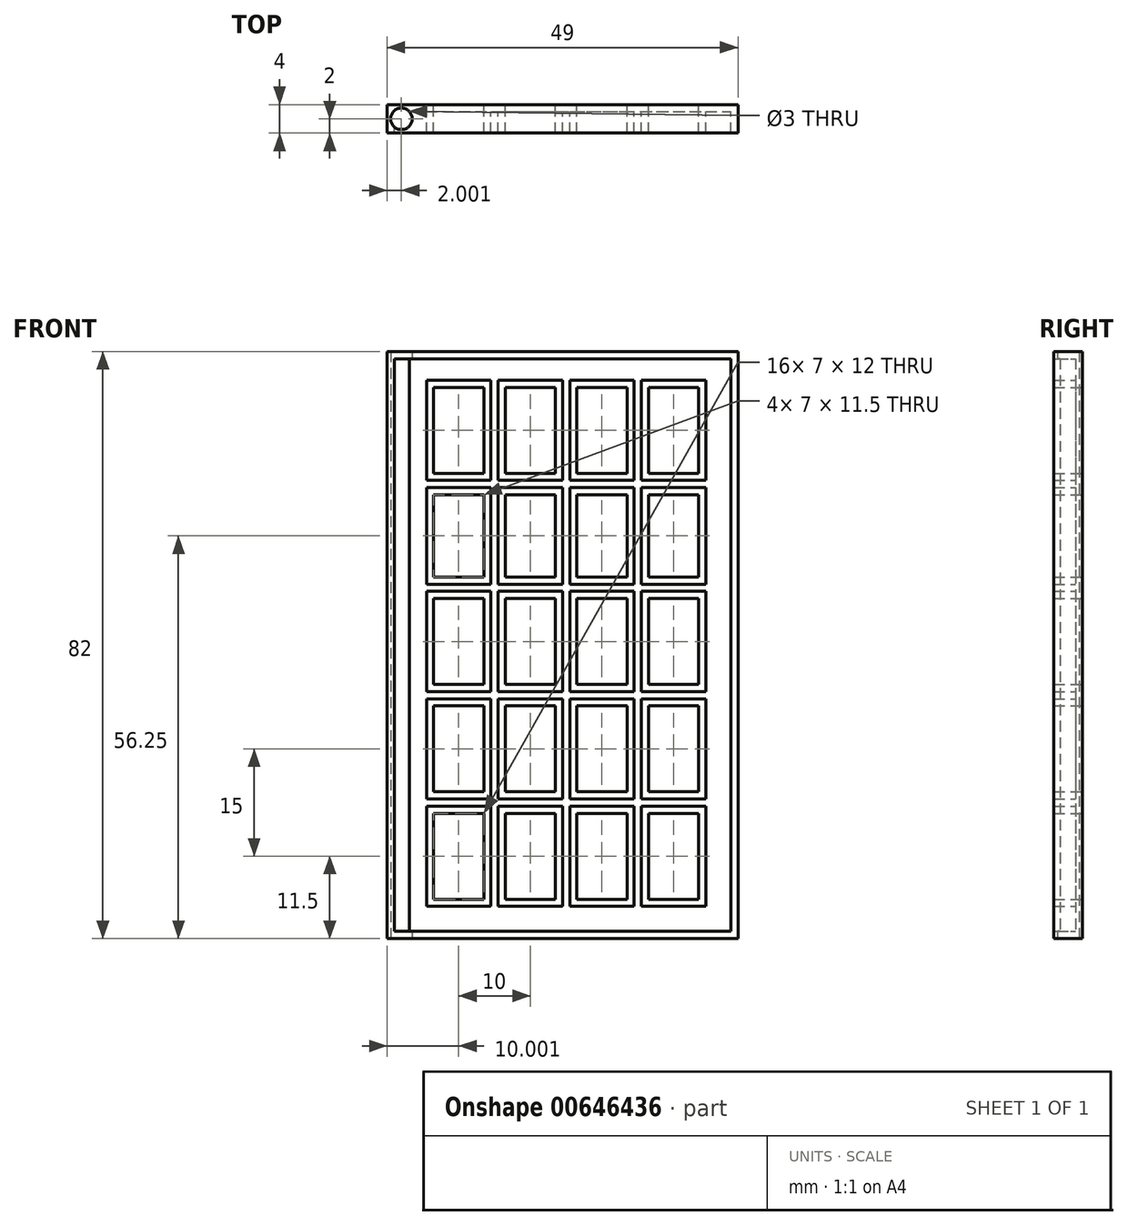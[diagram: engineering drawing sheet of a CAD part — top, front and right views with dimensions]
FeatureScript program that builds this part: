
annotation { "Feature Type Name" : "Feature", "Feature Type Description" : "" }
export const myFeature = defineFeature(function(context is Context, id is Id, definition is map)
    precondition{}
    {
        {
            var Q0;
            Q0=qCreatedBy(makeId("Front.planeOp"),FACE);
            var sketch = newSketch(context, id + "F0", { "sketchPlane" : qUnion([Q0])});
            skLineSegment(sketch, "E0.bottom", {"start": v(9.11, 82) * mm, "end": v(58.11, 82) * mm});
            skLineSegment(sketch, "E0.top", {"start": v(9.11, 0) * mm, "end": v(58.11, 0) * mm});
            skLineSegment(sketch, "E0.left", {"start": v(9.11, 82) * mm, "end": v(9.11, 0) * mm});
            skLineSegment(sketch, "E0.right", {"start": v(58.11, 82) * mm, "end": v(58.11, 0) * mm});
            skLineSegment(sketch, "E1.bottom", {"start": v(14.11, 78) * mm, "end": v(54.11, 78) * mm});
            skLineSegment(sketch, "E1.top", {"start": v(14.11, 4) * mm, "end": v(54.11, 4) * mm});
            skLineSegment(sketch, "E1.left", {"start": v(14.11, 78) * mm, "end": v(14.11, 4) * mm});
            skLineSegment(sketch, "E1.right", {"start": v(54.11, 78) * mm, "end": v(54.11, 4) * mm});
            skLineSegment(sketch, "E2.bottom", {"start": v(25.61, 77) * mm, "end": v(32.61, 77) * mm});
            skLineSegment(sketch, "E2.top", {"start": v(25.61, 65) * mm, "end": v(32.61, 65) * mm});
            skLineSegment(sketch, "E2.left", {"start": v(25.61, 77) * mm, "end": v(25.61, 65) * mm});
            skLineSegment(sketch, "E2.right", {"start": v(32.61, 77) * mm, "end": v(32.61, 65) * mm});
            skLineSegment(sketch, "E3.bottom", {"start": v(35.61, 77) * mm, "end": v(42.61, 77) * mm});
            skLineSegment(sketch, "E3.top", {"start": v(35.61, 65) * mm, "end": v(42.61, 65) * mm});
            skLineSegment(sketch, "E3.left", {"start": v(35.61, 77) * mm, "end": v(35.61, 65) * mm});
            skLineSegment(sketch, "E3.right", {"start": v(42.61, 77) * mm, "end": v(42.61, 65) * mm});
            skLineSegment(sketch, "E4.bottom", {"start": v(45.61, 77) * mm, "end": v(52.61, 77) * mm});
            skLineSegment(sketch, "E4.top", {"start": v(45.61, 65) * mm, "end": v(52.61, 65) * mm});
            skLineSegment(sketch, "E4.left", {"start": v(45.61, 77) * mm, "end": v(45.61, 65) * mm});
            skLineSegment(sketch, "E4.right", {"start": v(52.61, 77) * mm, "end": v(52.61, 65) * mm});
            skLineSegment(sketch, "E5.bottom", {"start": v(15.61, 77) * mm, "end": v(22.61, 77) * mm});
            skLineSegment(sketch, "E5.top", {"start": v(15.61, 65) * mm, "end": v(22.61, 65) * mm});
            skLineSegment(sketch, "E5.left", {"start": v(15.61, 77) * mm, "end": v(15.61, 65) * mm});
            skLineSegment(sketch, "E5.right", {"start": v(22.61, 77) * mm, "end": v(22.61, 65) * mm});
            skLineSegment(sketch, "E6.bottom", {"start": v(15.61, 62) * mm, "end": v(22.61, 62) * mm});
            skLineSegment(sketch, "E6.top", {"start": v(15.61, 50.5) * mm, "end": v(22.61, 50.5) * mm});
            skLineSegment(sketch, "E6.left", {"start": v(15.61, 62) * mm, "end": v(15.61, 50.5) * mm});
            skLineSegment(sketch, "E6.right", {"start": v(22.61, 62) * mm, "end": v(22.61, 50.5) * mm});
            skLineSegment(sketch, "E7.bottom", {"start": v(25.61, 62) * mm, "end": v(32.61, 62) * mm});
            skLineSegment(sketch, "E7.top", {"start": v(25.61, 50.5) * mm, "end": v(32.61, 50.5) * mm});
            skLineSegment(sketch, "E7.left", {"start": v(25.61, 62) * mm, "end": v(25.61, 50.5) * mm});
            skLineSegment(sketch, "E7.right", {"start": v(32.61, 62) * mm, "end": v(32.61, 50.5) * mm});
            skLineSegment(sketch, "E8.bottom", {"start": v(35.61, 62) * mm, "end": v(42.61, 62) * mm});
            skLineSegment(sketch, "E8.top", {"start": v(35.61, 50.5) * mm, "end": v(42.61, 50.5) * mm});
            skLineSegment(sketch, "E8.left", {"start": v(35.61, 62) * mm, "end": v(35.61, 50.5) * mm});
            skLineSegment(sketch, "E8.right", {"start": v(42.61, 62) * mm, "end": v(42.61, 50.5) * mm});
            skLineSegment(sketch, "E9.bottom", {"start": v(45.61, 62) * mm, "end": v(52.61, 62) * mm});
            skLineSegment(sketch, "E9.top", {"start": v(45.61, 50.5) * mm, "end": v(52.61, 50.5) * mm});
            skLineSegment(sketch, "E9.left", {"start": v(45.61, 62) * mm, "end": v(45.61, 50.5) * mm});
            skLineSegment(sketch, "E9.right", {"start": v(52.61, 62) * mm, "end": v(52.61, 50.5) * mm});
            skLineSegment(sketch, "E10.bottom", {"start": v(15.61, 47.5) * mm, "end": v(22.61, 47.5) * mm});
            skLineSegment(sketch, "E10.top", {"start": v(15.61, 35.5) * mm, "end": v(22.61, 35.5) * mm});
            skLineSegment(sketch, "E10.left", {"start": v(15.61, 47.5) * mm, "end": v(15.61, 35.5) * mm});
            skLineSegment(sketch, "E10.right", {"start": v(22.61, 47.5) * mm, "end": v(22.61, 35.5) * mm});
            skLineSegment(sketch, "E11.bottom", {"start": v(25.61, 47.5) * mm, "end": v(32.61, 47.5) * mm});
            skLineSegment(sketch, "E11.top", {"start": v(25.61, 35.5) * mm, "end": v(32.61, 35.5) * mm});
            skLineSegment(sketch, "E11.left", {"start": v(25.61, 47.5) * mm, "end": v(25.61, 35.5) * mm});
            skLineSegment(sketch, "E11.right", {"start": v(32.61, 47.5) * mm, "end": v(32.61, 35.5) * mm});
            skLineSegment(sketch, "E12.bottom", {"start": v(35.61, 47.5) * mm, "end": v(42.61, 47.5) * mm});
            skLineSegment(sketch, "E12.top", {"start": v(35.61, 35.5) * mm, "end": v(42.61, 35.5) * mm});
            skLineSegment(sketch, "E12.left", {"start": v(35.61, 47.5) * mm, "end": v(35.61, 35.5) * mm});
            skLineSegment(sketch, "E12.right", {"start": v(42.61, 47.5) * mm, "end": v(42.61, 35.5) * mm});
            skLineSegment(sketch, "E13.bottom", {"start": v(45.61, 47.5) * mm, "end": v(52.61, 47.5) * mm});
            skLineSegment(sketch, "E13.top", {"start": v(45.61, 35.5) * mm, "end": v(52.61, 35.5) * mm});
            skLineSegment(sketch, "E13.left", {"start": v(45.61, 47.5) * mm, "end": v(45.61, 35.5) * mm});
            skLineSegment(sketch, "E13.right", {"start": v(52.61, 47.5) * mm, "end": v(52.61, 35.5) * mm});
            skLineSegment(sketch, "E14.bottom", {"start": v(15.61, 32.5) * mm, "end": v(22.61, 32.5) * mm});
            skLineSegment(sketch, "E14.top", {"start": v(15.61, 20.5) * mm, "end": v(22.61, 20.5) * mm});
            skLineSegment(sketch, "E14.left", {"start": v(15.61, 32.5) * mm, "end": v(15.61, 20.5) * mm});
            skLineSegment(sketch, "E14.right", {"start": v(22.61, 32.5) * mm, "end": v(22.61, 20.5) * mm});
            skLineSegment(sketch, "E15.bottom", {"start": v(25.61, 32.5) * mm, "end": v(32.61, 32.5) * mm});
            skLineSegment(sketch, "E15.top", {"start": v(25.61, 20.5) * mm, "end": v(32.61, 20.5) * mm});
            skLineSegment(sketch, "E15.left", {"start": v(25.61, 32.5) * mm, "end": v(25.61, 20.5) * mm});
            skLineSegment(sketch, "E15.right", {"start": v(32.61, 32.5) * mm, "end": v(32.61, 20.5) * mm});
            skLineSegment(sketch, "E16.bottom", {"start": v(35.61, 32.5) * mm, "end": v(42.61, 32.5) * mm});
            skLineSegment(sketch, "E16.top", {"start": v(35.61, 20.5) * mm, "end": v(42.61, 20.5) * mm});
            skLineSegment(sketch, "E16.left", {"start": v(35.61, 32.5) * mm, "end": v(35.61, 20.5) * mm});
            skLineSegment(sketch, "E16.right", {"start": v(42.61, 32.5) * mm, "end": v(42.61, 20.5) * mm});
            skLineSegment(sketch, "E17.bottom", {"start": v(45.61, 32.5) * mm, "end": v(52.61, 32.5) * mm});
            skLineSegment(sketch, "E17.top", {"start": v(45.61, 20.5) * mm, "end": v(52.61, 20.5) * mm});
            skLineSegment(sketch, "E17.left", {"start": v(45.61, 32.5) * mm, "end": v(45.61, 20.5) * mm});
            skLineSegment(sketch, "E17.right", {"start": v(52.61, 32.5) * mm, "end": v(52.61, 20.5) * mm});
            skLineSegment(sketch, "E18.bottom", {"start": v(15.61, 17.5) * mm, "end": v(22.61, 17.5) * mm});
            skLineSegment(sketch, "E18.top", {"start": v(15.61, 5.5) * mm, "end": v(22.61, 5.5) * mm});
            skLineSegment(sketch, "E18.left", {"start": v(15.61, 17.5) * mm, "end": v(15.61, 5.5) * mm});
            skLineSegment(sketch, "E18.right", {"start": v(22.61, 17.5) * mm, "end": v(22.61, 5.5) * mm});
            skLineSegment(sketch, "E19.bottom", {"start": v(25.61, 17.5) * mm, "end": v(32.61, 17.5) * mm});
            skLineSegment(sketch, "E19.top", {"start": v(25.61, 5.5) * mm, "end": v(32.61, 5.5) * mm});
            skLineSegment(sketch, "E19.left", {"start": v(25.61, 17.5) * mm, "end": v(25.61, 5.5) * mm});
            skLineSegment(sketch, "E19.right", {"start": v(32.61, 17.5) * mm, "end": v(32.61, 5.5) * mm});
            skLineSegment(sketch, "E20.bottom", {"start": v(35.61, 17.5) * mm, "end": v(42.61, 17.5) * mm});
            skLineSegment(sketch, "E20.top", {"start": v(35.61, 5.5) * mm, "end": v(42.61, 5.5) * mm});
            skLineSegment(sketch, "E20.left", {"start": v(35.61, 17.5) * mm, "end": v(35.61, 5.5) * mm});
            skLineSegment(sketch, "E20.right", {"start": v(42.61, 17.5) * mm, "end": v(42.61, 5.5) * mm});
            skLineSegment(sketch, "E21.bottom", {"start": v(45.61, 17.5) * mm, "end": v(52.61, 17.5) * mm});
            skLineSegment(sketch, "E21.top", {"start": v(45.61, 5.5) * mm, "end": v(52.61, 5.5) * mm});
            skLineSegment(sketch, "E21.left", {"start": v(45.61, 17.5) * mm, "end": v(45.61, 5.5) * mm});
            skLineSegment(sketch, "E21.right", {"start": v(52.61, 17.5) * mm, "end": v(52.61, 5.5) * mm});
            skSolve(sketch);
        }
        {
            var Q0;
            {var subQ0=sQuery(id+"F0.wireOp",EDGE,"95jugb8S-jBrk-O8sG-tFiF-yQ4KkkH1rrNL");Q0=makeQuery(id+"F0.imprint","IMPRINT",FACE,{"disambiguationData":[TD([[makeQuery(id+"F0.imprint","IMPRINT",EDGE,{"derivedFrom":subQ0}),-1.0]])]});}
            var Q1;
            {var subQ0=sQuery(id+"F0.wireOp",EDGE,"Lh07aYga-HaEd-fFaN-Omj2-mk0DnxkQiKFK");Q1=makeQuery(id+"F0.imprint","IMPRINT",FACE,{"disambiguationData":[TD([[makeQuery(id+"F0.imprint","IMPRINT",EDGE,{"derivedFrom":subQ0}),1.0]])]});}
            var Q2;
            {var subQ0=sQuery(id+"F0.wireOp",EDGE,"E1.bottom");Q2=makeQuery(id+"F0.imprint","IMPRINT",FACE,{"disambiguationData":[TD([[makeQuery(id+"F0.imprint","IMPRINT",EDGE,{"derivedFrom":subQ0}),-1.0]])]});}
            var Q3;
            Q3=makeQuery(id+"F0.imprint","IMPRINT",FACE,{"disambiguationData":[TD([[makeQuery(id+"F0.imprint","IMPRINT",EDGE,{"derivedFrom":sQuery(id+"F0.wireOp",EDGE,"E0.bottom")}),-1.0]])]});
            extrude(context, id + "F1", {"entities" : qUnion([Q0, Q1, Q2, Q3]), "depth" : 4 * mm, "offsetDistance" : 25 * mm});
        }
        {
            var Q0;
            Q0=makeQuery(id+"F1.opExtrude","CAP_FACE",FACE,{"disambiguationData":[OSD([sQuery(id+"F0.wireOp",EDGE,"E0.bottom"),sQuery(id+"F0.wireOp",EDGE,"E0.top"),sQuery(id+"F0.wireOp",EDGE,"E0.left"),sQuery(id+"F0.wireOp",EDGE,"E0.right"),sQuery(id+"F0.wireOp",EDGE,"Lh07aYga-HaEd-fFaN-Omj2-mk0DnxkQiKFK"),sQuery(id+"F0.wireOp",EDGE,"c4zedJkT-ppuT-bWFh-VTKy-cviFX3TnlQdF"),sQuery(id+"F0.wireOp",EDGE,"6akIsR9Q-HoFu-n0Rd-93EP-QZRmaGRxVGNi"),sQuery(id+"F0.wireOp",EDGE,"95jugb8S-jBrk-O8sG-tFiF-yQ4KkkH1rrNL"),sQuery(id+"F0.wireOp",EDGE,"VLdeGPgl-wSv4-qNYT-lf8u-5PVO8Ypbj9SE"),sQuery(id+"F0.wireOp",EDGE,"bsdm5HnH-wmHM-gQTj-nhbf-ckwIAmanzvB3"),sQuery(id+"F0.wireOp",EDGE,"E2.bottom"),sQuery(id+"F0.wireOp",EDGE,"E2.top"),sQuery(id+"F0.wireOp",EDGE,"E2.left"),sQuery(id+"F0.wireOp",EDGE,"E2.right"),sQuery(id+"F0.wireOp",EDGE,"E3.bottom"),sQuery(id+"F0.wireOp",EDGE,"E3.top"),sQuery(id+"F0.wireOp",EDGE,"E3.left"),sQuery(id+"F0.wireOp",EDGE,"E3.right"),sQuery(id+"F0.wireOp",EDGE,"E4.bottom"),sQuery(id+"F0.wireOp",EDGE,"E4.top"),sQuery(id+"F0.wireOp",EDGE,"E4.left"),sQuery(id+"F0.wireOp",EDGE,"E4.right"),sQuery(id+"F0.wireOp",EDGE,"E5.bottom"),sQuery(id+"F0.wireOp",EDGE,"E5.top"),sQuery(id+"F0.wireOp",EDGE,"E5.left"),sQuery(id+"F0.wireOp",EDGE,"E5.right"),sQuery(id+"F0.wireOp",EDGE,"E6.bottom"),sQuery(id+"F0.wireOp",EDGE,"E6.top"),sQuery(id+"F0.wireOp",EDGE,"E6.left"),sQuery(id+"F0.wireOp",EDGE,"E6.right"),sQuery(id+"F0.wireOp",EDGE,"E7.bottom"),sQuery(id+"F0.wireOp",EDGE,"E7.top"),sQuery(id+"F0.wireOp",EDGE,"E7.left"),sQuery(id+"F0.wireOp",EDGE,"E7.right"),sQuery(id+"F0.wireOp",EDGE,"E8.bottom"),sQuery(id+"F0.wireOp",EDGE,"E8.top"),sQuery(id+"F0.wireOp",EDGE,"E8.left"),sQuery(id+"F0.wireOp",EDGE,"E8.right"),sQuery(id+"F0.wireOp",EDGE,"E9.bottom"),sQuery(id+"F0.wireOp",EDGE,"E9.top"),sQuery(id+"F0.wireOp",EDGE,"E9.left"),sQuery(id+"F0.wireOp",EDGE,"E9.right"),sQuery(id+"F0.wireOp",EDGE,"E10.bottom"),sQuery(id+"F0.wireOp",EDGE,"E10.top"),sQuery(id+"F0.wireOp",EDGE,"E10.left"),sQuery(id+"F0.wireOp",EDGE,"E10.right"),sQuery(id+"F0.wireOp",EDGE,"E11.bottom"),sQuery(id+"F0.wireOp",EDGE,"E11.top"),sQuery(id+"F0.wireOp",EDGE,"E11.left"),sQuery(id+"F0.wireOp",EDGE,"E11.right"),sQuery(id+"F0.wireOp",EDGE,"E12.bottom"),sQuery(id+"F0.wireOp",EDGE,"E12.top"),sQuery(id+"F0.wireOp",EDGE,"E12.left"),sQuery(id+"F0.wireOp",EDGE,"E12.right"),sQuery(id+"F0.wireOp",EDGE,"E13.bottom"),sQuery(id+"F0.wireOp",EDGE,"E13.top"),sQuery(id+"F0.wireOp",EDGE,"E13.left"),sQuery(id+"F0.wireOp",EDGE,"E13.right"),sQuery(id+"F0.wireOp",EDGE,"E14.bottom"),sQuery(id+"F0.wireOp",EDGE,"E14.top"),sQuery(id+"F0.wireOp",EDGE,"E14.left"),sQuery(id+"F0.wireOp",EDGE,"E14.right"),sQuery(id+"F0.wireOp",EDGE,"E15.bottom"),sQuery(id+"F0.wireOp",EDGE,"E15.top"),sQuery(id+"F0.wireOp",EDGE,"E15.left"),sQuery(id+"F0.wireOp",EDGE,"E15.right"),sQuery(id+"F0.wireOp",EDGE,"E16.bottom"),sQuery(id+"F0.wireOp",EDGE,"E16.top"),sQuery(id+"F0.wireOp",EDGE,"E16.left"),sQuery(id+"F0.wireOp",EDGE,"E16.right"),sQuery(id+"F0.wireOp",EDGE,"E17.bottom"),sQuery(id+"F0.wireOp",EDGE,"E17.top"),sQuery(id+"F0.wireOp",EDGE,"E17.left"),sQuery(id+"F0.wireOp",EDGE,"E17.right"),sQuery(id+"F0.wireOp",EDGE,"E18.bottom"),sQuery(id+"F0.wireOp",EDGE,"E18.top"),sQuery(id+"F0.wireOp",EDGE,"E18.left"),sQuery(id+"F0.wireOp",EDGE,"E18.right"),sQuery(id+"F0.wireOp",EDGE,"E19.bottom"),sQuery(id+"F0.wireOp",EDGE,"E19.top"),sQuery(id+"F0.wireOp",EDGE,"E19.left"),sQuery(id+"F0.wireOp",EDGE,"E19.right"),sQuery(id+"F0.wireOp",EDGE,"E20.bottom"),sQuery(id+"F0.wireOp",EDGE,"E20.top"),sQuery(id+"F0.wireOp",EDGE,"E20.left"),sQuery(id+"F0.wireOp",EDGE,"E20.right"),sQuery(id+"F0.wireOp",EDGE,"E21.bottom"),sQuery(id+"F0.wireOp",EDGE,"E21.top"),sQuery(id+"F0.wireOp",EDGE,"E21.left"),sQuery(id+"F0.wireOp",EDGE,"E21.right")])],"isStart":false});
            shell(context, id + "F2", {"entities" : qUnion([Q0]), "thickness" : 1 * mm});
        }
        {
            var Q0;
            Q0=qCreatedBy(makeId("Top.planeOp"),FACE);
            var sketch = newSketch(context, id + "F3", { "sketchPlane" : qUnion([Q0])});
            skPoint(sketch, "E22", {"position": v(11.11, -2) * mm});
            skSolve(sketch);
        }
        {
            var Q0;
            Q0=sQuery(id+"F3.wireOp",VERTEX,"E22");
            var Q1;
            Q1=makeQuery(id+"F1.opExtrude","SWEPT_BODY",BODY,{"disambiguationData":[OSD([sQuery(id+"F0.wireOp",EDGE,"E0.bottom"),sQuery(id+"F0.wireOp",EDGE,"E0.top"),sQuery(id+"F0.wireOp",EDGE,"E0.left"),sQuery(id+"F0.wireOp",EDGE,"E0.right"),sQuery(id+"F0.wireOp",EDGE,"E2.bottom"),sQuery(id+"F0.wireOp",EDGE,"E2.top"),sQuery(id+"F0.wireOp",EDGE,"E2.left"),sQuery(id+"F0.wireOp",EDGE,"E2.right"),sQuery(id+"F0.wireOp",EDGE,"E3.bottom"),sQuery(id+"F0.wireOp",EDGE,"E3.top"),sQuery(id+"F0.wireOp",EDGE,"E3.left"),sQuery(id+"F0.wireOp",EDGE,"E3.right"),sQuery(id+"F0.wireOp",EDGE,"E4.bottom"),sQuery(id+"F0.wireOp",EDGE,"E4.top"),sQuery(id+"F0.wireOp",EDGE,"E4.left"),sQuery(id+"F0.wireOp",EDGE,"E4.right"),sQuery(id+"F0.wireOp",EDGE,"E5.bottom"),sQuery(id+"F0.wireOp",EDGE,"E5.top"),sQuery(id+"F0.wireOp",EDGE,"E5.left"),sQuery(id+"F0.wireOp",EDGE,"E5.right"),sQuery(id+"F0.wireOp",EDGE,"E6.bottom"),sQuery(id+"F0.wireOp",EDGE,"E6.top"),sQuery(id+"F0.wireOp",EDGE,"E6.left"),sQuery(id+"F0.wireOp",EDGE,"E6.right"),sQuery(id+"F0.wireOp",EDGE,"E7.bottom"),sQuery(id+"F0.wireOp",EDGE,"E7.top"),sQuery(id+"F0.wireOp",EDGE,"E7.left"),sQuery(id+"F0.wireOp",EDGE,"E7.right"),sQuery(id+"F0.wireOp",EDGE,"E8.bottom"),sQuery(id+"F0.wireOp",EDGE,"E8.top"),sQuery(id+"F0.wireOp",EDGE,"E8.left"),sQuery(id+"F0.wireOp",EDGE,"E8.right"),sQuery(id+"F0.wireOp",EDGE,"E9.bottom"),sQuery(id+"F0.wireOp",EDGE,"E9.top"),sQuery(id+"F0.wireOp",EDGE,"E9.left"),sQuery(id+"F0.wireOp",EDGE,"E9.right"),sQuery(id+"F0.wireOp",EDGE,"E10.bottom"),sQuery(id+"F0.wireOp",EDGE,"E10.top"),sQuery(id+"F0.wireOp",EDGE,"E10.left"),sQuery(id+"F0.wireOp",EDGE,"E10.right"),sQuery(id+"F0.wireOp",EDGE,"E11.bottom"),sQuery(id+"F0.wireOp",EDGE,"E11.top"),sQuery(id+"F0.wireOp",EDGE,"E11.left"),sQuery(id+"F0.wireOp",EDGE,"E11.right"),sQuery(id+"F0.wireOp",EDGE,"E12.bottom"),sQuery(id+"F0.wireOp",EDGE,"E12.top"),sQuery(id+"F0.wireOp",EDGE,"E12.left"),sQuery(id+"F0.wireOp",EDGE,"E12.right"),sQuery(id+"F0.wireOp",EDGE,"E13.bottom"),sQuery(id+"F0.wireOp",EDGE,"E13.top"),sQuery(id+"F0.wireOp",EDGE,"E13.left"),sQuery(id+"F0.wireOp",EDGE,"E13.right"),sQuery(id+"F0.wireOp",EDGE,"E14.bottom"),sQuery(id+"F0.wireOp",EDGE,"E14.top"),sQuery(id+"F0.wireOp",EDGE,"E14.left"),sQuery(id+"F0.wireOp",EDGE,"E14.right"),sQuery(id+"F0.wireOp",EDGE,"E15.bottom"),sQuery(id+"F0.wireOp",EDGE,"E15.top"),sQuery(id+"F0.wireOp",EDGE,"E15.left"),sQuery(id+"F0.wireOp",EDGE,"E15.right"),sQuery(id+"F0.wireOp",EDGE,"E16.bottom"),sQuery(id+"F0.wireOp",EDGE,"E16.top"),sQuery(id+"F0.wireOp",EDGE,"E16.left"),sQuery(id+"F0.wireOp",EDGE,"E16.right"),sQuery(id+"F0.wireOp",EDGE,"E17.bottom"),sQuery(id+"F0.wireOp",EDGE,"E17.top"),sQuery(id+"F0.wireOp",EDGE,"E17.left"),sQuery(id+"F0.wireOp",EDGE,"E17.right"),sQuery(id+"F0.wireOp",EDGE,"E18.bottom"),sQuery(id+"F0.wireOp",EDGE,"E18.top"),sQuery(id+"F0.wireOp",EDGE,"E18.left"),sQuery(id+"F0.wireOp",EDGE,"E18.right"),sQuery(id+"F0.wireOp",EDGE,"E19.bottom"),sQuery(id+"F0.wireOp",EDGE,"E19.top"),sQuery(id+"F0.wireOp",EDGE,"E19.left"),sQuery(id+"F0.wireOp",EDGE,"E19.right"),sQuery(id+"F0.wireOp",EDGE,"E20.bottom"),sQuery(id+"F0.wireOp",EDGE,"E20.top"),sQuery(id+"F0.wireOp",EDGE,"E20.left"),sQuery(id+"F0.wireOp",EDGE,"E20.right"),sQuery(id+"F0.wireOp",EDGE,"E21.bottom"),sQuery(id+"F0.wireOp",EDGE,"E21.top"),sQuery(id+"F0.wireOp",EDGE,"E21.left"),sQuery(id+"F0.wireOp",EDGE,"E21.right")])]});
            hole(context, id + "F4", {"style" : HoleStyle.SIMPLE, "endStyle" : HoleEndStyle.THROUGH, "oppositeDirection" : true, "holeDiameter" : 3 * mm, "majorDiameter" : 5 * mm, "isTappedThrough" : true, "tappedDepth" : 12 * mm, "tapClearance" : 3, "locations" : qUnion([Q0]), "scope" : qUnion([Q1])});
        }
    });
